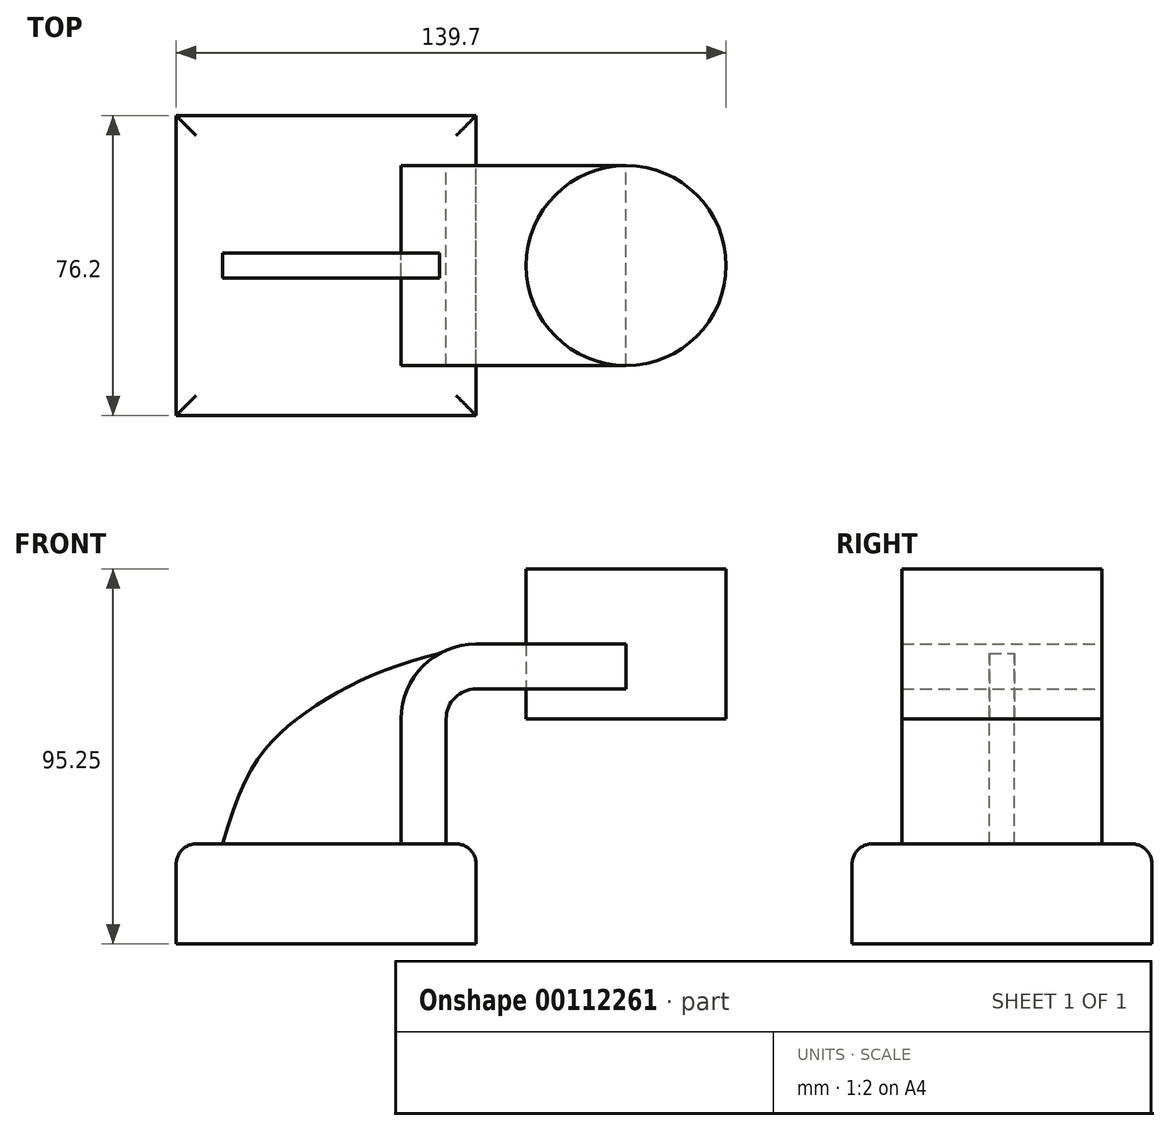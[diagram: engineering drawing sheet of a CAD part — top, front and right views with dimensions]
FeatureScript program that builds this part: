
annotation { "Feature Type Name" : "Feature", "Feature Type Description" : "" }
export const myFeature = defineFeature(function(context is Context, id is Id, definition is map)
    precondition{}
    {
        {
            var Q0;
            Q0=qCreatedBy(makeId("Front.planeOp"),FACE);
            var sketch = newSketch(context, id + "F0", { "sketchPlane" : qUnion([Q0])});
            skLineSegment(sketch, "E0.bottom", {"start": v(38.1, 12.7) * mm, "end": v(-38.1, 12.7) * mm});
            skLineSegment(sketch, "E0.top", {"start": v(38.1, -12.7) * mm, "end": v(-38.1, -12.7) * mm});
            skLineSegment(sketch, "E0.left", {"start": v(38.1, 12.7) * mm, "end": v(38.1, -12.7) * mm});
            skLineSegment(sketch, "E0.right", {"start": v(-38.1, 12.7) * mm, "end": v(-38.1, -12.7) * mm});
            skPoint(sketch, "E0.middle", {"position": v(0, 0) * mm});
            skLineSegment(sketch, "E1.bottom", {"start": v(76.2, 44.45) * mm, "end": v(127, 44.45) * mm});
            skLineSegment(sketch, "E1.top", {"start": v(76.2, 82.55) * mm, "end": v(127, 82.55) * mm});
            skLineSegment(sketch, "E1.left", {"start": v(76.2, 44.45) * mm, "end": v(76.2, 82.55) * mm});
            skLineSegment(sketch, "E1.right", {"start": v(127, 44.45) * mm, "end": v(127, 82.55) * mm});
            skPoint(sketch, "E1.middle", {"position": v(101.6, 63.5) * mm});
            skLineSegment(sketch, "E2", {"start": v(19.05, 12.7) * mm, "end": v(19.05, 44.45) * mm});
            skLineSegment(sketch, "E3", {"start": v(76.2, 63.5) * mm, "end": v(38.1, 63.5) * mm});
            skPoint(sketch, "E3.endSnap0", {"position": v(76.2, 63.5) * mm});
            skArc(sketch, "E4", {"start": v(19.05, 44.45) * mm, "mid": v(24.63, 57.92) * mm, "end": v(38.1, 63.5) * mm});
            skFitSpline(sketch, "E5", {"points": [v(-26.27, 12.7) * mm, v(-6.31, 45.26) * mm, v(28.79, 61.07) * mm], "startDerivative": vector(29.85, 112.31) * mm, "endDerivative": vector(82.42, 18.35) * mm});
            skLineSegment(sketch, "E6.0", {"start": v(76.2, 52.07) * mm, "end": v(38.1, 52.07) * mm});
            skArc(sketch, "E6.1", {"start": v(30.48, 44.45) * mm, "mid": v(32.71, 49.84) * mm, "end": v(38.1, 52.07) * mm});
            skLineSegment(sketch, "E6.2", {"start": v(30.48, 12.7) * mm, "end": v(30.48, 44.45) * mm});
            skLineSegment(sketch, "E7", {"start": v(101.6, 44.45) * mm, "end": v(101.6, 82.55) * mm});
            skSolve(sketch);
        }
        {
            var Q0;
            Q0=makeQuery(id+"F0.imprint","IMPRINT",FACE,{"disambiguationData":[TD([[makeQuery(id+"F0.imprint","IMPRINT",EDGE,{"derivedFrom":sQuery(id+"F0.wireOp",EDGE,"E0.top")}),-1.0]])]});
            extrude(context, id + "F1", {"entities" : qUnion([Q0]), "endBound" : BoundingType.SYMMETRIC, "depth" : 76.2 * mm});
        }
        {
            var Q0;
            {var subQ2=sQuery(id+"F0.wireOp",EDGE,"E2");Q0=makeQuery(id+"F0.imprint","IMPRINT",FACE,{"disambiguationData":[TD([[makeQuery(id+"F0.imprint","IMPRINT",EDGE,{"derivedFrom":subQ2}),-1.0]])]});}
            extrude(context, id + "F2", {"entities" : qUnion([Q0]), "operationType" : NewBodyOperationType.ADD, "endBound" : BoundingType.SYMMETRIC, "depth" : 50.8 * mm});
        }
        {
            var Q0;
            {var subQ7=sQuery(id+"F0.wireOp",EDGE,"E7");Q0=makeQuery(id+"F0.imprint","IMPRINT",FACE,{"disambiguationData":[TD([[makeQuery(id+"F0.imprint","IMPRINT",EDGE,{"derivedFrom":subQ7}),1.0]])]});}
            var Q1;
            Q1=sQuery(id+"F0.wireOp",EDGE,"E1.left");
            revolve(context, id + "F3", {"entities" : qUnion([Q0]), "axis" : qUnion([Q1]), "revolveType" : RevolveType.FULL});
        }
        {
            var Q0;
            {var subQ0=sQuery(id+"F0.wireOp",EDGE,"E2");Q0=makeQuery(id+"F0.imprint","IMPRINT",FACE,{"disambiguationData":[TD([[makeQuery(id+"F0.imprint","IMPRINT",EDGE,{"derivedFrom":subQ0}),1.0]])]});}
            extrude(context, id + "F4", {"entities" : qUnion([Q0]), "endBound" : BoundingType.SYMMETRIC, "depth" : 6.35 * mm});
        }
        {
            var Q0;
            Q0=makeQuery(id+"F1.opExtrude","SWEPT_EDGE",EDGE,{"disambiguationData":[OSD([sQuery(id+"F0.wireOp",EDGE,"E0.bottom"),sQuery(id+"F0.wireOp",EDGE,"E0.right")])]});
            var Q1;
            Q1=makeQuery(id+"F1.opExtrude","CAP_EDGE",EDGE,{"disambiguationData":[OSD([sQuery(id+"F0.wireOp",EDGE,"E0.bottom")])],"isStart":true});
            var Q2;
            Q2=makeQuery(id+"F1.opExtrude","SWEPT_EDGE",EDGE,{"disambiguationData":[OSD([sQuery(id+"F0.wireOp",EDGE,"E0.bottom"),sQuery(id+"F0.wireOp",EDGE,"E0.left")])]});
            var Q3;
            Q3=makeQuery(id+"F1.opExtrude","CAP_EDGE",EDGE,{"disambiguationData":[OSD([sQuery(id+"F0.wireOp",EDGE,"E0.bottom")])],"isStart":false});
            fillet(context, id + "F5", {"entities" : qUnion([Q0, Q1, Q2, Q3]), "radius" : 5.08 * mm, "tangentPropagation" : true, "allowEdgeOverflow" : false});
        }
    });
